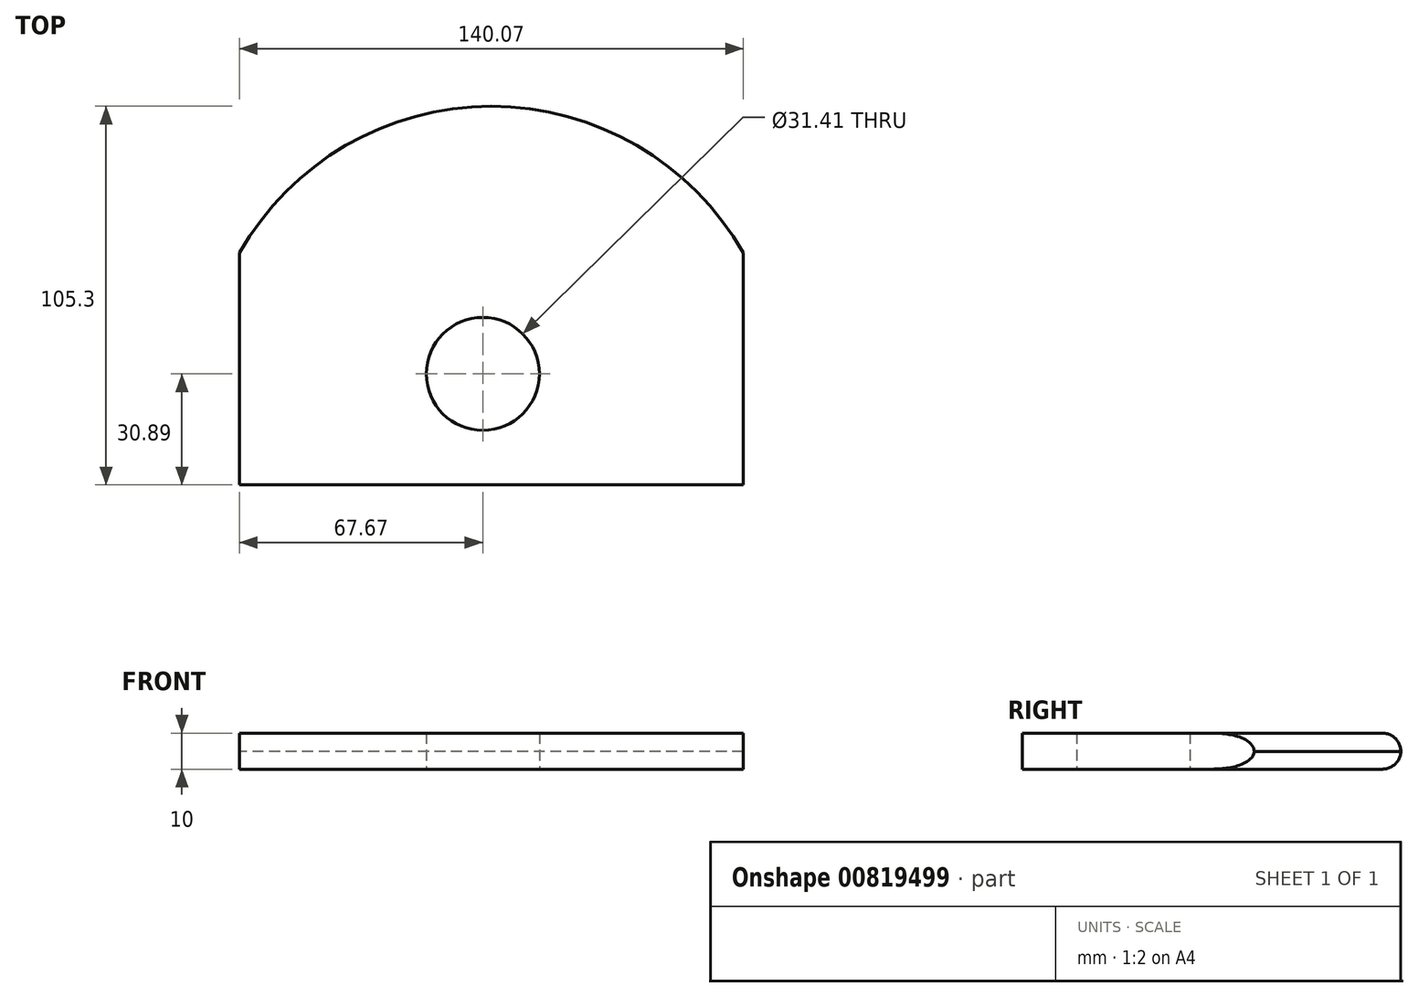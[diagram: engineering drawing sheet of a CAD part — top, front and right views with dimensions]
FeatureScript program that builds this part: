
annotation { "Feature Type Name" : "Feature", "Feature Type Description" : "" }
export const myFeature = defineFeature(function(context is Context, id is Id, definition is map)
    precondition{}
    {
        {
            var Q0;
            Q0=qCreatedBy(makeId("Top.planeOp"),FACE);
            var sketch = newSketch(context, id + "F0", { "sketchPlane" : qUnion([Q0])});
            skLineSegment(sketch, "E0.top", {"start": v(-67.67, -30.89) * mm, "end": v(72.4, -30.89) * mm});
            skLineSegment(sketch, "E0.left", {"start": v(-67.67, 33.64) * mm, "end": v(-67.67, -30.89) * mm});
            skLineSegment(sketch, "E0.right", {"start": v(72.4, 33.64) * mm, "end": v(72.4, -30.89) * mm});
            skArc(sketch, "E1", {"start": v(72.4, 33.64) * mm, "mid": v(2.36, 74.4) * mm, "end": v(-67.67, 33.64) * mm});
            skCircle(sketch, "E2", {"center": v(0, 0) * mm, "radius": 15.7 * mm});
            skSolve(sketch);
        }
        {
            var Q0;
            Q0=makeQuery(id+"F0.imprint","IMPRINT",FACE,{"disambiguationData":[TD([[makeQuery(id+"F0.imprint","IMPRINT",EDGE,{"derivedFrom":sQuery(id+"F0.wireOp",EDGE,"E0.top")}),1.0]])]});
            extrude(context, id + "F1", {"entities" : qUnion([Q0]), "depth" : 10 * mm, "offsetDistance" : 25.4 * mm});
        }
        {
            var Q0;
            Q0=makeQuery(id+"F1.opExtrude","CAP_EDGE",EDGE,{"disambiguationData":[OSD([sQuery(id+"F0.wireOp",EDGE,"E1")])],"isStart":false});
            fillet(context, id + "F2", {"entities" : qUnion([Q0]), "radius" : 5.08 * mm, "tangentPropagation" : true, "allowEdgeOverflow" : false});
        }
        {
            var Q0;
            Q0=makeQuery(id+"F1.opExtrude","CAP_EDGE",EDGE,{"disambiguationData":[OSD([sQuery(id+"F0.wireOp",EDGE,"E1")])],"isStart":true});
            fillet(context, id + "F3", {"entities" : qUnion([Q0]), "radius" : 5.08 * mm, "tangentPropagation" : true, "allowEdgeOverflow" : false});
        }
    });
